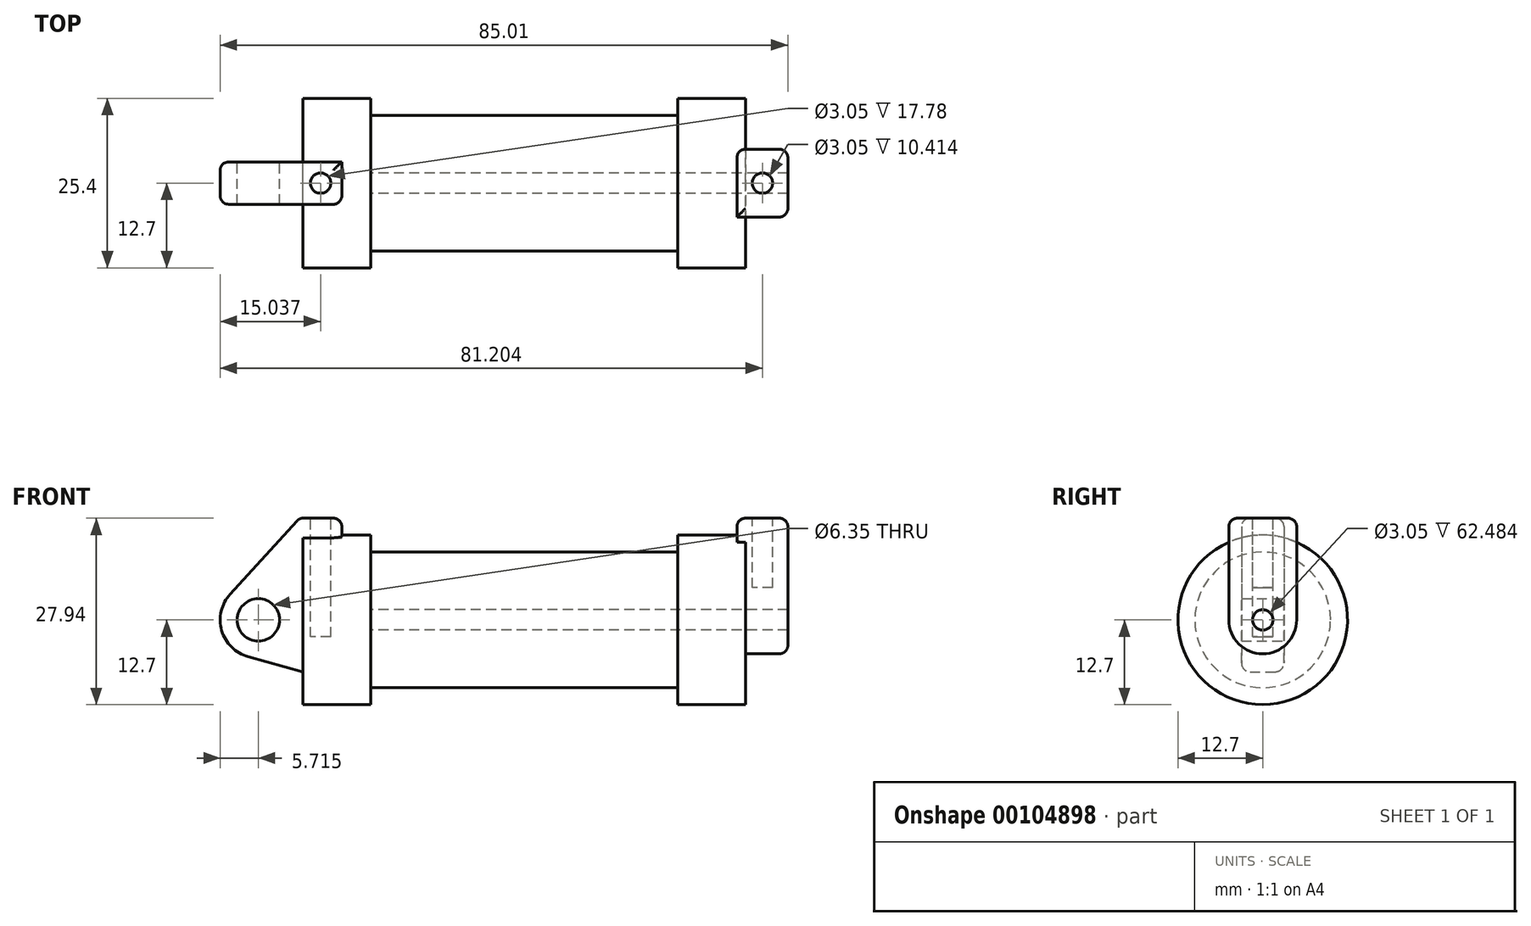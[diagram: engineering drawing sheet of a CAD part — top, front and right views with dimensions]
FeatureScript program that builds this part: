
annotation { "Feature Type Name" : "Feature", "Feature Type Description" : "" }
export const myFeature = defineFeature(function(context is Context, id is Id, definition is map)
    precondition{}
    {
        {
            var Q0;
            Q0=qCreatedBy(makeId("Front.planeOp"),FACE);
            var sketch = newSketch(context, id + "F0", { "sketchPlane" : qUnion([Q0])});
            skLineSegment(sketch, "E0", {"start": v(0, 0) * mm, "end": v(0, 12.7) * mm});
            skLineSegment(sketch, "E1", {"start": v(0, 12.7) * mm, "end": v(10.16, 12.7) * mm});
            skLineSegment(sketch, "E2", {"start": v(10.16, 12.7) * mm, "end": v(10.16, 10.16) * mm});
            skLineSegment(sketch, "E3", {"start": v(10.16, 10.16) * mm, "end": v(56.13, 10.16) * mm});
            skLineSegment(sketch, "E4", {"start": v(56.13, 10.16) * mm, "end": v(56.13, 12.7) * mm});
            skLineSegment(sketch, "E5", {"start": v(56.13, 12.7) * mm, "end": v(66.3, 12.7) * mm});
            skLineSegment(sketch, "E6", {"start": v(66.3, 12.7) * mm, "end": v(66.3, 0) * mm});
            skLineSegment(sketch, "E7", {"start": v(66.3, 0) * mm, "end": v(0, 0) * mm});
            skLineSegment(sketch, "E8", {"start": v(5.84, 15.24) * mm, "end": v(-0.5, 15.24) * mm});
            skLineSegment(sketch, "E9", {"start": v(-0.5, 15.24) * mm, "end": v(-10.88, 3.85) * mm});
            skLineSegment(sketch, "E10", {"start": v(0, 0) * mm, "end": v(-6.65, 0) * mm});
            skCircle(sketch, "E11", {"center": v(-6.65, 0) * mm, "radius": 5.72 * mm});
            skCircle(sketch, "E12", {"center": v(-6.65, 0) * mm, "radius": 3.18 * mm});
            skLineSegment(sketch, "E13", {"start": v(5.84, 15.24) * mm, "end": v(5.84, -9.4) * mm});
            skLineSegment(sketch, "E14", {"start": v(5.84, -9.4) * mm, "end": v(-8.18, -5.5) * mm});
            skSolve(sketch);
        }
        {
            var Q0;
            {var subQ0=sQuery(id+"F0.wireOp",EDGE,"E2");Q0=makeQuery(id+"F0.imprint","IMPRINT",FACE,{"disambiguationData":[TD([[makeQuery(id+"F0.imprint","IMPRINT",EDGE,{"derivedFrom":subQ0}),-1.0]])]});}
            var Q1;
            {var subQ0=sQuery(id+"F0.wireOp",EDGE,"E0");Q1=makeQuery(id+"F0.imprint","IMPRINT",FACE,{"disambiguationData":[TD([[makeQuery(id+"F0.imprint","IMPRINT",EDGE,{"derivedFrom":subQ0}),-1.0]])]});}
            var Q2;
            Q2=sQuery(id+"F0.wireOp",EDGE,"E7");
            revolve(context, id + "F1", {"entities" : qUnion([Q0, Q1]), "axis" : qUnion([Q2]), "revolveType" : RevolveType.FULL});
        }
        {
            var Q0;
            {var subQ0=sQuery(id+"F0.wireOp",EDGE,"E0");Q0=makeQuery(id+"F0.imprint","IMPRINT",FACE,{"disambiguationData":[TD([[makeQuery(id+"F0.imprint","IMPRINT",EDGE,{"derivedFrom":subQ0}),-1.0]])]});}
            var Q1;
            {var subQ3=sQuery(id+"F0.wireOp",EDGE,"E0");Q1=makeQuery(id+"F0.imprint","IMPRINT",FACE,{"disambiguationData":[TD([[makeQuery(id+"F0.imprint","IMPRINT",EDGE,{"derivedFrom":subQ3}),1.0]])]});}
            var Q2;
            {var subQ4=sQuery(id+"F0.wireOp",EDGE,"E12");Q2=makeQuery(id+"F0.imprint","IMPRINT",FACE,{"disambiguationData":[TD([[makeQuery(id+"F0.imprint","IMPRINT",EDGE,{"derivedFrom":subQ4}),-1.0]])]});}
            var Q3;
            {var subQ0=sQuery(id+"F0.wireOp",EDGE,"E14");Q3=makeQuery(id+"F0.imprint","IMPRINT",FACE,{"disambiguationData":[TD([[makeQuery(id+"F0.imprint","IMPRINT",EDGE,{"derivedFrom":subQ0}),-1.0]])]});}
            extrude(context, id + "F2", {"entities" : qUnion([Q0, Q1, Q2, Q3]), "operationType" : NewBodyOperationType.ADD, "endBound" : BoundingType.SYMMETRIC, "depth" : 6.35 * mm});
        }
        {
            var Q0;
            Q0=makeQuery(id+"F1.opRevolve","SWEPT_FACE",FACE,{"disambiguationData":[OSD([sQuery(id+"F0.wireOp",EDGE,"E6")])]});
            var sketch = newSketch(context, id + "F3", { "sketchPlane" : qUnion([Q0])});
            skCircle(sketch, "E15", {"center": v(0, 0) * mm, "radius": 1.52 * mm});
            skCircle(sketch, "E16", {"center": v(0, 0) * mm, "radius": 5.08 * mm});
            skLineSegment(sketch, "E17", {"start": v(-5.08, 0) * mm, "end": v(-5.08, 15.24) * mm});
            skLineSegment(sketch, "E18", {"start": v(5.08, 0) * mm, "end": v(5.08, 15.24) * mm});
            skLineSegment(sketch, "E19", {"start": v(-5.08, 15.24) * mm, "end": v(5.08, 15.24) * mm});
            skSolve(sketch);
        }
        {
            var Q0;
            Q0 = qSketchRegion(id + "F3", true);
            extrude(context, id + "F4", {"entities" : qUnion([Q0]), "operationType" : NewBodyOperationType.ADD, "depth" : 6.35 * mm, "hasSecondDirection" : true, "secondDirectionOppositeDirection" : true, "secondDirectionDepth" : 1.27 * mm});
        }
        {
            var Q0;
            Q0=makeQuery(id+"F4.opExtrude","SWEPT_FACE",FACE,{"disambiguationData":[OSD([sQuery(id+"F3.wireOp",EDGE,"E19")])]});
            var sketch = newSketch(context, id + "F5", { "sketchPlane" : qUnion([Q0])});
            skCircle(sketch, "E20", {"center": v(68.83, 0) * mm, "radius": 1.52 * mm});
            skPoint(sketch, "E20.centerSnap0", {"position": v(72.64, 0) * mm});
            skPoint(sketch, "E20.centerSnap1", {"position": v(68.83, 5.08) * mm});
            skSolve(sketch);
        }
        {
            var Q0;
            Q0=makeQuery(id+"F2.opExtrude","SWEPT_FACE",FACE,{"disambiguationData":[OSD([sQuery(id+"F0.wireOp",EDGE,"E8")])]});
            var sketch = newSketch(context, id + "F6", { "sketchPlane" : qUnion([Q0])});
            skCircle(sketch, "E21", {"center": v(2.67, 0) * mm, "radius": 1.52 * mm});
            skPoint(sketch, "E21.centerSnap0", {"position": v(5.84, 0) * mm});
            skPoint(sketch, "E21.centerSnap1", {"position": v(2.67, 3.18) * mm});
            skSolve(sketch);
        }
        {
            var Q0;
            Q0=makeQuery(id+"F6.imprint","IMPRINT",FACE,{"disambiguationData":[TD([[makeQuery(id+"F6.imprint","IMPRINT",EDGE,{"derivedFrom":sQuery(id+"F6.wireOp",EDGE,"E21")}),1.0]])]});
            extrude(context, id + "F7", {"entities" : qUnion([Q0]), "operationType" : NewBodyOperationType.REMOVE, "oppositeDirection" : true, "depth" : 17.78 * mm});
        }
        {
            var Q0;
            Q0=makeQuery(id+"F5.imprint","IMPRINT",FACE,{"disambiguationData":[TD([[makeQuery(id+"F5.imprint","IMPRINT",EDGE,{"derivedFrom":sQuery(id+"F5.wireOp",EDGE,"E20")}),1.0]])]});
            extrude(context, id + "F8", {"entities" : qUnion([Q0]), "operationType" : NewBodyOperationType.REMOVE, "oppositeDirection" : true, "depth" : 10.4 * mm});
        }
        {
            var Q0;
            Q0=makeQuery(id+"F3.imprint","IMPRINT",FACE,{"disambiguationData":[TD([[makeQuery(id+"F3.imprint","IMPRINT",EDGE,{"derivedFrom":sQuery(id+"F3.wireOp",EDGE,"E15")}),1.0]])]});
            var Q1;
            Q1=makeQuery(id+"F1.opRevolve","SWEPT_FACE",FACE,{"disambiguationData":[OSD([sQuery(id+"F0.wireOp",EDGE,"E2")])]});
            extrude(context, id + "F9", {"entities" : qUnion([Q0]), "operationType" : NewBodyOperationType.REMOVE, "endBound" : BoundingType.UP_TO_SURFACE, "oppositeDirection" : true, "endBoundEntityFace" : qUnion([Q1]), "depth" : 25.4 * mm});
        }
        {
            var Q0;
            Q0=makeQuery(id+"F4.opExtrude","CAP_EDGE",EDGE,{"disambiguationData":[OSD([sQuery(id+"F3.wireOp",EDGE,"E18")])],"isStart":true});
            var Q1;
            Q1=makeQuery(id+"F4.opExtrude","CAP_EDGE",EDGE,{"disambiguationData":[OSD([sQuery(id+"F3.wireOp",EDGE,"E19")])],"isStart":true});
            var Q2;
            Q2=makeQuery(id+"F4.opExtrude","SWEPT_EDGE",EDGE,{"disambiguationData":[OSD([sQuery(id+"F3.wireOp",EDGE,"E18"),sQuery(id+"F3.wireOp",EDGE,"E19")])]});
            var Q3;
            Q3=makeQuery(id+"F4.opExtrude","CAP_EDGE",EDGE,{"disambiguationData":[OSD([sQuery(id+"F3.wireOp",EDGE,"E19")])],"isStart":false});
            var Q4;
            Q4=makeQuery(id+"F4.opExtrude","SWEPT_EDGE",EDGE,{"disambiguationData":[OSD([sQuery(id+"F3.wireOp",EDGE,"E17"),sQuery(id+"F3.wireOp",EDGE,"E19")])]});
            var Q5;
            Q5=makeQuery(id+"F4.opExtrude","CAP_EDGE",EDGE,{"disambiguationData":[OSD([sQuery(id+"F3.wireOp",EDGE,"E18")])],"isStart":false});
            var Q6;
            Q6=makeQuery(id+"F4.opExtrude","CAP_EDGE",EDGE,{"disambiguationData":[OSD([sQuery(id+"F3.wireOp",EDGE,"E17")])],"isStart":false});
            var Q7;
            Q7=makeQuery(id+"F2.opExtrude","CAP_EDGE",EDGE,{"disambiguationData":[OSD([sQuery(id+"F0.wireOp",EDGE,"E8")])],"isStart":true});
            var Q8;
            Q8=makeQuery(id+"F2.opExtrude","CAP_EDGE",EDGE,{"disambiguationData":[OSD([sQuery(id+"F0.wireOp",EDGE,"E9")])],"isStart":true});
            var Q9;
            Q9=makeQuery(id+"F2.opExtrude","SWEPT_EDGE",EDGE,{"disambiguationData":[OSD([sQuery(id+"F0.wireOp",EDGE,"E8"),sQuery(id+"F0.wireOp",EDGE,"E13")])]});
            var Q10;
            Q10=makeQuery(id+"F2.opExtrude","CAP_EDGE",EDGE,{"disambiguationData":[OSD([sQuery(id+"F0.wireOp",EDGE,"E8")])],"isStart":false});
            var Q11;
            Q11=makeQuery(id+"F2.opExtrude","CAP_EDGE",EDGE,{"disambiguationData":[OSD([sQuery(id+"F0.wireOp",EDGE,"E13")])],"isStart":false});
            var Q12;
            Q12=makeQuery(id+"F2.opExtrude","SWEPT_EDGE",EDGE,{"disambiguationData":[OSD([sQuery(id+"F0.wireOp",EDGE,"E8"),sQuery(id+"F0.wireOp",EDGE,"E9")])]});
            var Q13;
            Q13=makeQuery(id+"F2.opExtrude","CAP_EDGE",EDGE,{"disambiguationData":[OSD([sQuery(id+"F0.wireOp",EDGE,"E9")])],"isStart":false});
            fillet(context, id + "F10", {"entities" : qUnion([Q0, Q1, Q2, Q3, Q4, Q5, Q6, Q7, Q8, Q9, Q10, Q11, Q12, Q13]), "radius" : 1.27 * mm, "tangentPropagation" : true, "allowEdgeOverflow" : false});
        }
    });
